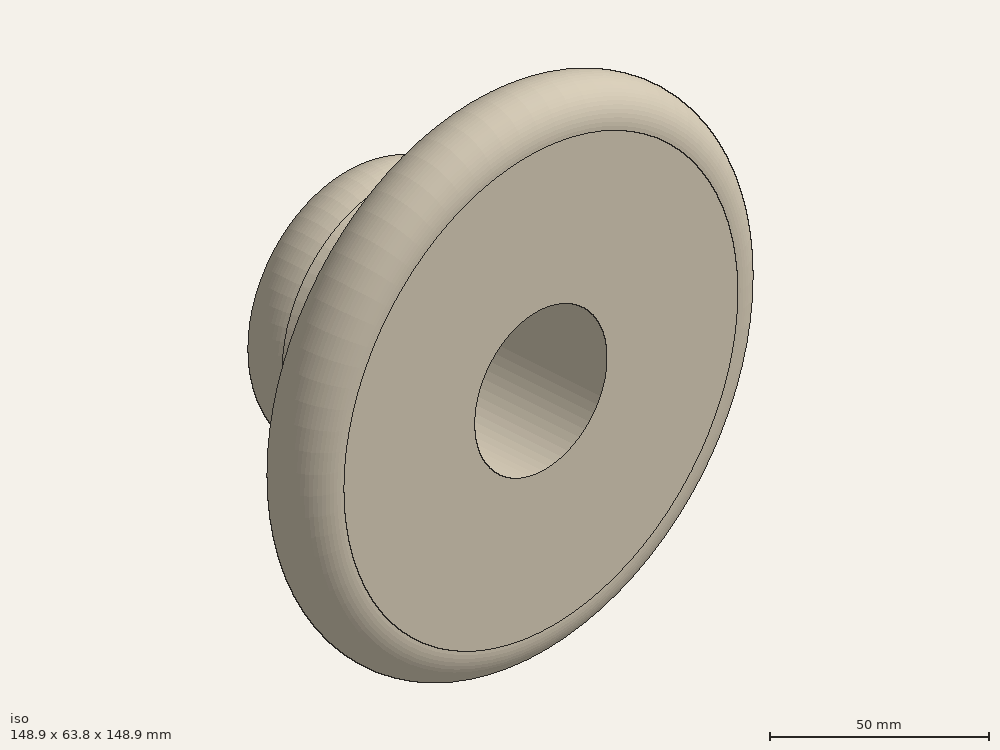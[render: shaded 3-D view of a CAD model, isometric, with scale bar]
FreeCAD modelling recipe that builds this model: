
FCSTD DOCUMENT  (FreeCAD 1.1R20260108 (Git shallow))
Label: Sketcher_ArcOfHyperbola
License: Public Domain
LicenseURL: https://en.wikipedia.org/wiki/Public_domain
objects: App::Point×1, Sketcher::SketchObject×1, PartDesign::Revolution×1, PartDesign::Body×1
note: 6 computed .brp shape members not serialized (recipe doc carries the construction recipe); baked Part::Feature solids carry a one-line shape summary decoded from their .brp

FEATURE [App::Point] Origin001
  Role = Origin
FEATURE [Sketcher::SketchObject] Sketch
  ArcFitTolerance = 1e-06
  AttachmentSupport = -> [Origin]
  ExternalTypes = [0]
  FullyConstrained = true
  MakeInternals = false
  MapMode = 5
  sketch-geometry (9):
    g0: ArcOfHyperbola CenterX=0 CenterY=0 CenterZ=0 NormalX=0 NormalY=0 NormalZ=1 MajorRadius=30 MinorRadius=12.5 AngleXU=2.61799 StartAngle=-1.10817 EndAngle=1.33239
    g1: LineSegment [constr] StartX=-25.9808 StartY=15 StartZ=0 EndX=25.9808 EndY=-15 EndZ=0
    g2: LineSegment [constr] StartX=-32.2308 StartY=4.17469 StartZ=0 EndX=-19.7308 EndY=25.8253 EndZ=0
    g3: GeomPoint [constr] X=-28.1458 Y=16.25 Z=0
    g4: LineSegment [constr] StartX=-75 StartY=0 StartZ=0 EndX=0 EndY=75 EndZ=0
    g5: ArcOfCircle CenterX=-26.7753 CenterY=45.1849 CenterZ=0 NormalX=0 NormalY=0 NormalZ=1 AngleXU=0 Radius=10 StartAngle=1.00203 EndAngle=3.71036
    g6: ArcOfCircle CenterX=-64.4498 CenterY=1.34772 CenterZ=0 NormalX=0 NormalY=0 NormalZ=1 AngleXU=0 Radius=10 StartAngle=1.49392 EndAngle=4.78927
    g7: LineSegment StartX=-63.6818 StartY=-8.62274 StartZ=0 EndX=-21.3894 EndY=-8.62274 EndZ=0
    g8: LineSegment StartX=-21.3894 StartY=-8.62274 StartZ=0 EndX=-21.3894 EndY=53.6106 EndZ=0
  constraints (24):
    c: InternalAlignment(g1,g0)
    c: InternalAlignment(g2,g0)
    c: InternalAlignment(g3,g0)
    c: Coincident(g0,g-1)
    c: Angle(g1,g-1) = 0.523599
    c: Distance(g2,g2) = 25
    c: Distance(g1,g1) = 60
    c: PointOnObject(g4,g-1)
    c: PointOnObject(g4,g-2)
    c: Angle(g4,g-1) = 2.35619
    c: PointOnObject(g0,g4)
    c: PointOnObject(g0,g4)
    c: PointOnObject(g5,g4)
    c: Tangent(g5,g0) = -1.5708
    c: Tangent(g6,g0) = -1.5708
    c: DistanceX(g4,g0) = 75
    c: Equal(g5,g6)
    c: Radius(g6) = 10
    c: Coincident(g7,g6)
    c: Horizontal(g7)
    c: Coincident(g8,g7)
    c: Coincident(g8,g5)
    c: Vertical(g8)
    c: Vertical(g6,g0)
FEATURE [PartDesign::Revolution] Revolution
  Angle = 360
  Angle2 = 0
  Axis = (0,1,0)
  Base = (0,0,0)
  FuseOrder = 0
  Profile = -> Sketch
  ReferenceAxis = -> Sketch [V_Axis]
  Refine = true
  Suppressed = false
  Type = 0
FEATURE [PartDesign::Body] Body
  AllowCompound = true
  Group = -> [Sketch,Revolution]
  Origin = -> Origin
  Tip = -> Revolution
